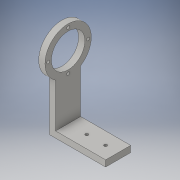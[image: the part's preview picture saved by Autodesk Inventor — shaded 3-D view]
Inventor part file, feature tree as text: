
AUTODESK INVENTOR PART (.ipt)
format: ipt  version: 2016 (Build 200138000, 138)  size: 141,312 bytes
history: native  units: in
note: dims shown in document units (in); Inventor stores cm internally (conversion verified against a paired STEP export)
features: extrude x4, sketch x4
ambient origin geometry x8: Origin, YZ Plane, XZ Plane, XY Plane, X Axis, Y Axis, Z Axis, Center Point
bodies: Solid1 (feature_tree)
feature tree (8):
  extrude  "Extrusion1"  Depth=1.34in
  extrude  "Extrusion2"  Depth=0.25in TaperAngle=0.0deg
  extrude  "Extrusion3"  Depth=2.0in TaperAngle=0.0deg
  extrude  "Extrusion4"  Depth=2.0in
  sketch  "Sketch1"  dims[d0=0.255in d1=1.34in]
  sketch  "Sketch2"  dims[d7=1.0in d8=0.25in d9=0.0in]
  sketch  "Sketch3"  dims[d10=0.25in d11=2.0in d12=0.0in]
  sketch  "Sketch4"  dims[d14=0.5in d15=0.5in d16=0.1181in d17=0.1181in d18=0.5in d19=1.0in d20=2.0in d21=0.0in d22=0.1181in d23=1.5748in d25=360.0deg d27=2.0in d28=0.0in]
